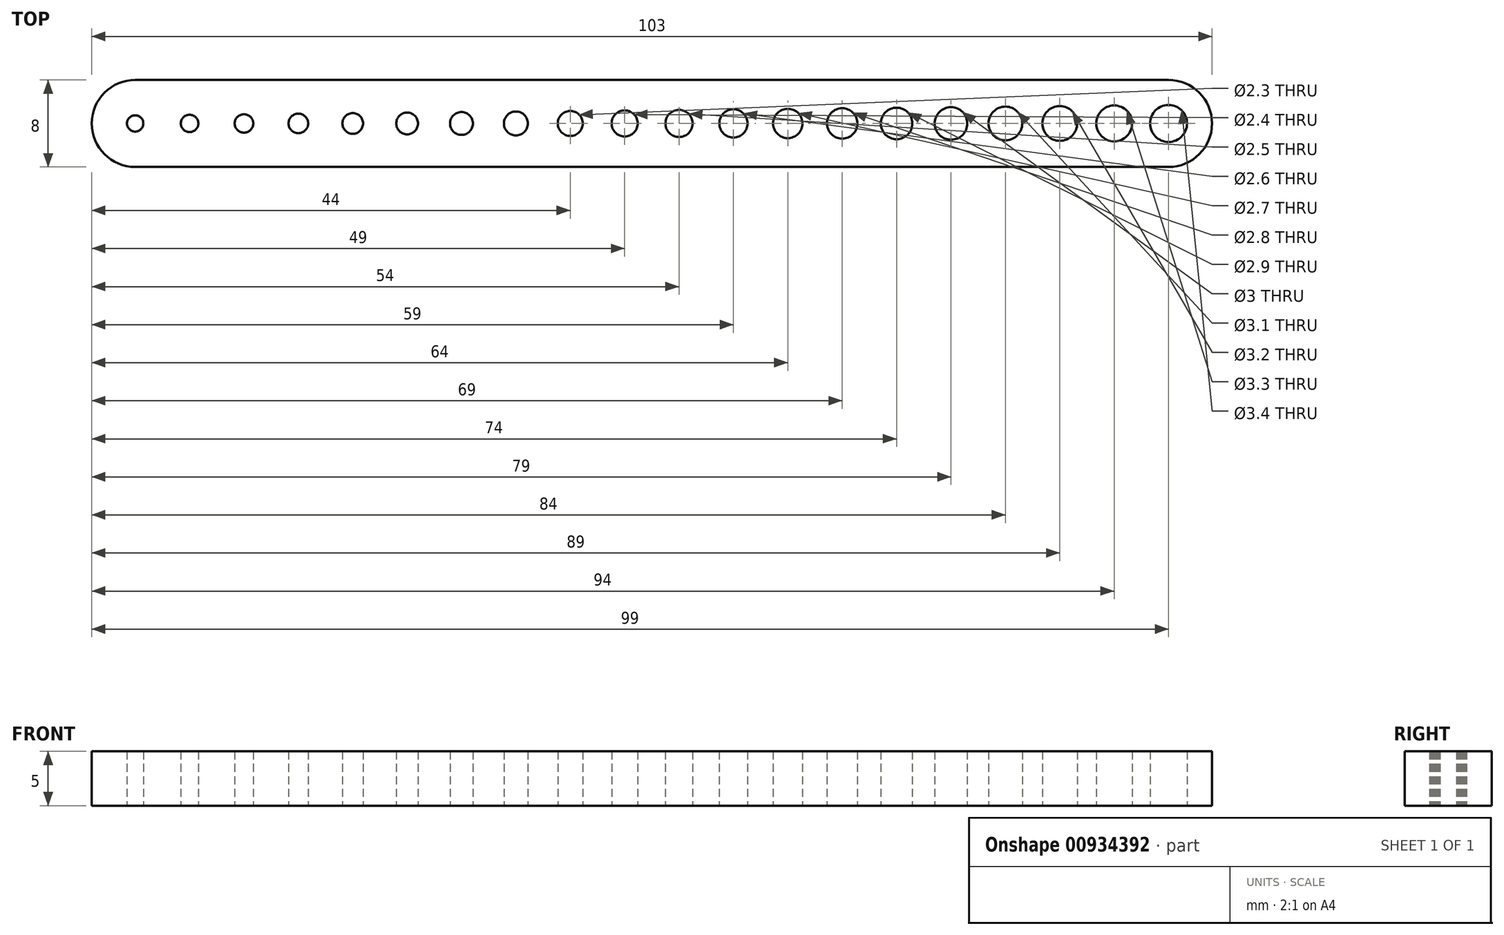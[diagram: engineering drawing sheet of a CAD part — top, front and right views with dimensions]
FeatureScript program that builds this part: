
annotation { "Feature Type Name" : "Feature", "Feature Type Description" : "" }
export const myFeature = defineFeature(function(context is Context, id is Id, definition is map)
    precondition{}
    {
        {
            var Q0;
            Q0=qCreatedBy(makeId("Top.planeOp"),FACE);
            var sketch = newSketch(context, id + "F0", { "sketchPlane" : qUnion([Q0])});
            skLineSegment(sketch, "E0.bottom", {"start": v(4, 0) * mm, "end": v(99, 0) * mm});
            skLineSegment(sketch, "E0.top", {"start": v(4, 8) * mm, "end": v(99, 8) * mm});
            skLineSegment(sketch, "E0.left", {"start": v(0, 4) * mm, "end": v(0, 4) * mm});
            skLineSegment(sketch, "E0.right", {"start": v(103, 4) * mm, "end": v(103, 4) * mm});
            skPoint(sketch, "E1.visualSharp", {"position": v(0, 8) * mm});
            skArc(sketch, "E1.filletArc", {"start": v(4, 8) * mm, "mid": v(1.17, 6.83) * mm, "end": v(0, 4) * mm});
            skPoint(sketch, "E2.visualSharp", {"position": v(0, 0) * mm});
            skArc(sketch, "E2.filletArc", {"start": v(0, 4) * mm, "mid": v(1.17, 1.17) * mm, "end": v(4, 0) * mm});
            skPoint(sketch, "E3.visualSharp", {"position": v(103, 8) * mm});
            skArc(sketch, "E3.filletArc", {"start": v(103, 4) * mm, "mid": v(101.83, 6.83) * mm, "end": v(99, 8) * mm});
            skPoint(sketch, "E4.visualSharp", {"position": v(103, 0) * mm});
            skArc(sketch, "E4.filletArc", {"start": v(99, 0) * mm, "mid": v(101.83, 1.17) * mm, "end": v(103, 4) * mm});
            skLineSegment(sketch, "E5", {"start": v(99, 4) * mm, "end": v(4, 4) * mm, "construction": true});
            skLineSegment(sketch, "E6", {"start": v(4, 4) * mm, "end": v(9, 4) * mm, "construction": true});
            skLineSegment(sketch, "E7", {"start": v(9, 4) * mm, "end": v(14, 4) * mm, "construction": true});
            skLineSegment(sketch, "E8", {"start": v(14, 4) * mm, "end": v(19, 4) * mm, "construction": true});
            skLineSegment(sketch, "E9", {"start": v(19, 4) * mm, "end": v(24, 4) * mm, "construction": true});
            skLineSegment(sketch, "E10", {"start": v(24, 4) * mm, "end": v(29, 4) * mm, "construction": true});
            skLineSegment(sketch, "E11", {"start": v(29, 4) * mm, "end": v(34, 4) * mm, "construction": true});
            skLineSegment(sketch, "E12", {"start": v(34, 4) * mm, "end": v(39, 4) * mm, "construction": true});
            skLineSegment(sketch, "E13", {"start": v(39, 4) * mm, "end": v(44, 4) * mm, "construction": true});
            skLineSegment(sketch, "E14", {"start": v(44, 4) * mm, "end": v(49, 4) * mm, "construction": true});
            skLineSegment(sketch, "E15", {"start": v(49, 4) * mm, "end": v(54, 4) * mm, "construction": true});
            skLineSegment(sketch, "E16", {"start": v(54, 4) * mm, "end": v(59, 4) * mm, "construction": true});
            skLineSegment(sketch, "E17", {"start": v(59, 4) * mm, "end": v(64, 4) * mm, "construction": true});
            skLineSegment(sketch, "E18", {"start": v(64, 4) * mm, "end": v(69, 4) * mm, "construction": true});
            skLineSegment(sketch, "E19", {"start": v(69, 4) * mm, "end": v(74, 4) * mm, "construction": true});
            skLineSegment(sketch, "E20", {"start": v(74, 4) * mm, "end": v(79, 4) * mm, "construction": true});
            skLineSegment(sketch, "E21", {"start": v(79, 4) * mm, "end": v(84, 4) * mm, "construction": true});
            skLineSegment(sketch, "E22", {"start": v(84, 4) * mm, "end": v(89, 4) * mm, "construction": true});
            skLineSegment(sketch, "E23", {"start": v(89, 4) * mm, "end": v(94, 4) * mm, "construction": true});
            skCircle(sketch, "E24", {"center": v(4, 4) * mm, "radius": 0.75 * mm});
            skCircle(sketch, "E25", {"center": v(99, 4) * mm, "radius": 1.7 * mm});
            skLineSegment(sketch, "E26", {"start": v(99, 4) * mm, "end": v(99, 8) * mm, "construction": true});
            skLineSegment(sketch, "E27", {"start": v(94, 4) * mm, "end": v(94, 8) * mm, "construction": true});
            skLineSegment(sketch, "E28", {"start": v(94, 8) * mm, "end": v(89, 8) * mm});
            skLineSegment(sketch, "E29", {"start": v(89, 8) * mm, "end": v(89, 4) * mm, "construction": true});
            skLineSegment(sketch, "E30", {"start": v(84, 4) * mm, "end": v(84, 8) * mm, "construction": true});
            skLineSegment(sketch, "E31", {"start": v(84, 8) * mm, "end": v(79, 8) * mm});
            skLineSegment(sketch, "E32", {"start": v(79, 8) * mm, "end": v(79, 4) * mm, "construction": true});
            skLineSegment(sketch, "E33", {"start": v(74, 4) * mm, "end": v(74, 8) * mm, "construction": true});
            skLineSegment(sketch, "E34", {"start": v(74, 8) * mm, "end": v(69, 8) * mm});
            skLineSegment(sketch, "E35", {"start": v(69, 8) * mm, "end": v(69, 4) * mm, "construction": true});
            skLineSegment(sketch, "E36", {"start": v(64, 4) * mm, "end": v(64, 8) * mm, "construction": true});
            skLineSegment(sketch, "E37", {"start": v(64, 8) * mm, "end": v(59, 8) * mm});
            skLineSegment(sketch, "E38", {"start": v(59, 8) * mm, "end": v(59, 4) * mm, "construction": true});
            skLineSegment(sketch, "E39", {"start": v(54, 4) * mm, "end": v(54, 8) * mm, "construction": true});
            skLineSegment(sketch, "E40", {"start": v(54, 8) * mm, "end": v(49, 8) * mm});
            skLineSegment(sketch, "E41", {"start": v(49, 8) * mm, "end": v(49, 4) * mm, "construction": true});
            skLineSegment(sketch, "E42", {"start": v(44, 4) * mm, "end": v(44, 8) * mm, "construction": true});
            skLineSegment(sketch, "E43", {"start": v(44, 8) * mm, "end": v(39, 8) * mm});
            skLineSegment(sketch, "E44", {"start": v(39, 8) * mm, "end": v(39, 4) * mm, "construction": true});
            skLineSegment(sketch, "E45", {"start": v(34, 4) * mm, "end": v(34, 8) * mm, "construction": true});
            skLineSegment(sketch, "E46", {"start": v(34, 8) * mm, "end": v(29, 8) * mm});
            skLineSegment(sketch, "E47", {"start": v(29, 8) * mm, "end": v(29, 4) * mm, "construction": true});
            skLineSegment(sketch, "E48", {"start": v(24, 4) * mm, "end": v(24, 8) * mm, "construction": true});
            skLineSegment(sketch, "E49", {"start": v(24, 8) * mm, "end": v(19, 8) * mm});
            skLineSegment(sketch, "E50", {"start": v(19, 8) * mm, "end": v(19, 4) * mm, "construction": true});
            skLineSegment(sketch, "E51", {"start": v(14, 4) * mm, "end": v(14, 8) * mm, "construction": true});
            skLineSegment(sketch, "E52", {"start": v(14, 8) * mm, "end": v(9, 8) * mm});
            skLineSegment(sketch, "E53", {"start": v(9, 8) * mm, "end": v(9, 4) * mm, "construction": true});
            skLineSegment(sketch, "E54", {"start": v(4, 4) * mm, "end": v(4, 8) * mm, "construction": true});
            skLineSegment(sketch, "E55", {"start": v(4, 4.75) * mm, "end": v(99, 5.7) * mm, "construction": true});
            skCircle(sketch, "E56", {"center": v(94, 4) * mm, "radius": 1.65 * mm});
            skCircle(sketch, "E57", {"center": v(89, 4) * mm, "radius": 1.6 * mm});
            skCircle(sketch, "E58", {"center": v(84, 4) * mm, "radius": 1.55 * mm});
            skCircle(sketch, "E59", {"center": v(79, 4) * mm, "radius": 1.5 * mm});
            skCircle(sketch, "E60", {"center": v(74, 4) * mm, "radius": 1.45 * mm});
            skCircle(sketch, "E61", {"center": v(69, 4) * mm, "radius": 1.4 * mm});
            skCircle(sketch, "E62", {"center": v(64, 4) * mm, "radius": 1.35 * mm});
            skCircle(sketch, "E63", {"center": v(59, 4) * mm, "radius": 1.3 * mm});
            skCircle(sketch, "E64", {"center": v(54, 4) * mm, "radius": 1.25 * mm});
            skCircle(sketch, "E65", {"center": v(49, 4) * mm, "radius": 1.2 * mm});
            skCircle(sketch, "E66", {"center": v(44, 4) * mm, "radius": 1.15 * mm});
            skCircle(sketch, "E67", {"center": v(39, 4) * mm, "radius": 1.1 * mm});
            skCircle(sketch, "E68", {"center": v(34, 4) * mm, "radius": 1.05 * mm});
            skCircle(sketch, "E69", {"center": v(29, 4) * mm, "radius": 1 * mm});
            skCircle(sketch, "E70", {"center": v(24, 4) * mm, "radius": 0.95 * mm});
            skCircle(sketch, "E71", {"center": v(19, 4) * mm, "radius": 0.9 * mm});
            skCircle(sketch, "E72", {"center": v(14, 4) * mm, "radius": 0.85 * mm});
            skCircle(sketch, "E73", {"center": v(9, 4) * mm, "radius": 0.8 * mm});
            skSolve(sketch);
        }
        {
            var Q0;
            Q0 = qSketchRegion(id + "F0", true);
            var Q1;
            {var subQ0=sQuery(id+"F0.wireOp",EDGE,"E24");var subQ1=sQuery(id+"F0.wireOp",EDGE,"E6");var subQ2=makeQuery(id+"F0.imprint","INTERSECT",VERTEX,{"derivedFrom":[subQ1,subQ0]});Q1=makeQuery(id+"F0.imprint","IMPRINT",FACE,{"disambiguationData":[TD([[makeQuery(id+"F0.imprint","IMPRINT",EDGE,{"disambiguationData":[TD([[subQ2,-1.0]])],"derivedFrom":subQ1}),1.0]])]});}
            var Q2;
            {var subQ1=sQuery(id+"F0.wireOp",EDGE,"E7");var subQ7=sQuery(id+"F0.wireOp",EDGE,"E73");var subQ9=makeQuery(id+"F0.imprint","INTERSECT",VERTEX,{"derivedFrom":[subQ1,subQ7]});Q2=makeQuery(id+"F0.imprint","IMPRINT",FACE,{"disambiguationData":[TD([[makeQuery(id+"F0.imprint","IMPRINT",EDGE,{"disambiguationData":[TD([[subQ9,-1.0]])],"derivedFrom":subQ1}),1.0]])]});}
            var Q3;
            {var subQ5=sQuery(id+"F0.wireOp",EDGE,"E72");var subQ7=sQuery(id+"F0.wireOp",EDGE,"E8");var subQ8=makeQuery(id+"F0.imprint","INTERSECT",VERTEX,{"derivedFrom":[subQ7,subQ5]});Q3=makeQuery(id+"F0.imprint","IMPRINT",FACE,{"disambiguationData":[TD([[makeQuery(id+"F0.imprint","IMPRINT",EDGE,{"disambiguationData":[TD([[subQ8,-1.0]])],"derivedFrom":subQ7}),1.0]])]});}
            var Q4;
            {var subQ1=sQuery(id+"F0.wireOp",EDGE,"E9");var subQ7=sQuery(id+"F0.wireOp",EDGE,"E71");var subQ9=makeQuery(id+"F0.imprint","INTERSECT",VERTEX,{"derivedFrom":[subQ1,subQ7]});Q4=makeQuery(id+"F0.imprint","IMPRINT",FACE,{"disambiguationData":[TD([[makeQuery(id+"F0.imprint","IMPRINT",EDGE,{"disambiguationData":[TD([[subQ9,-1.0]])],"derivedFrom":subQ1}),1.0]])]});}
            var Q5;
            {var subQ1=sQuery(id+"F0.wireOp",EDGE,"E10");var subQ7=sQuery(id+"F0.wireOp",EDGE,"E70");var subQ9=makeQuery(id+"F0.imprint","INTERSECT",VERTEX,{"derivedFrom":[subQ1,subQ7]});Q5=makeQuery(id+"F0.imprint","IMPRINT",FACE,{"disambiguationData":[TD([[makeQuery(id+"F0.imprint","IMPRINT",EDGE,{"disambiguationData":[TD([[subQ9,-1.0]])],"derivedFrom":subQ1}),1.0]])]});}
            var Q6;
            {var subQ1=sQuery(id+"F0.wireOp",EDGE,"E11");var subQ7=sQuery(id+"F0.wireOp",EDGE,"E69");var subQ8=makeQuery(id+"F0.imprint","INTERSECT",VERTEX,{"derivedFrom":[subQ1,subQ7]});Q6=makeQuery(id+"F0.imprint","IMPRINT",FACE,{"disambiguationData":[TD([[makeQuery(id+"F0.imprint","IMPRINT",EDGE,{"disambiguationData":[TD([[subQ8,-1.0]])],"derivedFrom":subQ1}),1.0]])]});}
            var Q7;
            {var subQ1=sQuery(id+"F0.wireOp",EDGE,"E12");var subQ5=sQuery(id+"F0.wireOp",EDGE,"E68");var subQ9=makeQuery(id+"F0.imprint","INTERSECT",VERTEX,{"derivedFrom":[subQ1,subQ5]});Q7=makeQuery(id+"F0.imprint","IMPRINT",FACE,{"disambiguationData":[TD([[makeQuery(id+"F0.imprint","IMPRINT",EDGE,{"disambiguationData":[TD([[subQ9,-1.0]])],"derivedFrom":subQ1}),1.0]])]});}
            var Q8;
            {var subQ5=sQuery(id+"F0.wireOp",EDGE,"E13");var subQ7=sQuery(id+"F0.wireOp",EDGE,"E67");var subQ9=makeQuery(id+"F0.imprint","INTERSECT",VERTEX,{"derivedFrom":[subQ5,subQ7]});Q8=makeQuery(id+"F0.imprint","IMPRINT",FACE,{"disambiguationData":[TD([[makeQuery(id+"F0.imprint","IMPRINT",EDGE,{"disambiguationData":[TD([[subQ9,-1.0]])],"derivedFrom":subQ5}),1.0]])]});}
            var Q9;
            {var subQ1=sQuery(id+"F0.wireOp",EDGE,"E14");var subQ7=sQuery(id+"F0.wireOp",EDGE,"E66");var subQ9=makeQuery(id+"F0.imprint","INTERSECT",VERTEX,{"derivedFrom":[subQ1,subQ7]});Q9=makeQuery(id+"F0.imprint","IMPRINT",FACE,{"disambiguationData":[TD([[makeQuery(id+"F0.imprint","IMPRINT",EDGE,{"disambiguationData":[TD([[subQ9,-1.0]])],"derivedFrom":subQ1}),1.0]])]});}
            var Q10;
            {var subQ1=sQuery(id+"F0.wireOp",EDGE,"E15");var subQ7=sQuery(id+"F0.wireOp",EDGE,"E65");var subQ9=makeQuery(id+"F0.imprint","INTERSECT",VERTEX,{"derivedFrom":[subQ1,subQ7]});Q10=makeQuery(id+"F0.imprint","IMPRINT",FACE,{"disambiguationData":[TD([[makeQuery(id+"F0.imprint","IMPRINT",EDGE,{"disambiguationData":[TD([[subQ9,-1.0]])],"derivedFrom":subQ1}),1.0]])]});}
            var Q11;
            {var subQ1=sQuery(id+"F0.wireOp",EDGE,"E16");var subQ7=sQuery(id+"F0.wireOp",EDGE,"E64");var subQ9=makeQuery(id+"F0.imprint","INTERSECT",VERTEX,{"derivedFrom":[subQ1,subQ7]});Q11=makeQuery(id+"F0.imprint","IMPRINT",FACE,{"disambiguationData":[TD([[makeQuery(id+"F0.imprint","IMPRINT",EDGE,{"disambiguationData":[TD([[subQ9,-1.0]])],"derivedFrom":subQ1}),1.0]])]});}
            var Q12;
            {var subQ1=sQuery(id+"F0.wireOp",EDGE,"E17");var subQ7=sQuery(id+"F0.wireOp",EDGE,"E63");var subQ9=makeQuery(id+"F0.imprint","INTERSECT",VERTEX,{"derivedFrom":[subQ1,subQ7]});Q12=makeQuery(id+"F0.imprint","IMPRINT",FACE,{"disambiguationData":[TD([[makeQuery(id+"F0.imprint","IMPRINT",EDGE,{"disambiguationData":[TD([[subQ9,-1.0]])],"derivedFrom":subQ1}),1.0]])]});}
            var Q13;
            {var subQ5=sQuery(id+"F0.wireOp",EDGE,"E62");var subQ7=sQuery(id+"F0.wireOp",EDGE,"E18");var subQ9=makeQuery(id+"F0.imprint","INTERSECT",VERTEX,{"derivedFrom":[subQ7,subQ5]});Q13=makeQuery(id+"F0.imprint","IMPRINT",FACE,{"disambiguationData":[TD([[makeQuery(id+"F0.imprint","IMPRINT",EDGE,{"disambiguationData":[TD([[subQ9,-1.0]])],"derivedFrom":subQ7}),1.0]])]});}
            var Q14;
            {var subQ1=sQuery(id+"F0.wireOp",EDGE,"E19");var subQ5=sQuery(id+"F0.wireOp",EDGE,"E61");var subQ6=makeQuery(id+"F0.imprint","INTERSECT",VERTEX,{"derivedFrom":[subQ1,subQ5]});Q14=makeQuery(id+"F0.imprint","IMPRINT",FACE,{"disambiguationData":[TD([[makeQuery(id+"F0.imprint","IMPRINT",EDGE,{"disambiguationData":[TD([[subQ6,-1.0]])],"derivedFrom":subQ1}),1.0]])]});}
            var Q15;
            {var subQ1=sQuery(id+"F0.wireOp",EDGE,"E20");var subQ7=sQuery(id+"F0.wireOp",EDGE,"E60");var subQ9=makeQuery(id+"F0.imprint","INTERSECT",VERTEX,{"derivedFrom":[subQ1,subQ7]});Q15=makeQuery(id+"F0.imprint","IMPRINT",FACE,{"disambiguationData":[TD([[makeQuery(id+"F0.imprint","IMPRINT",EDGE,{"disambiguationData":[TD([[subQ9,-1.0]])],"derivedFrom":subQ1}),1.0]])]});}
            var Q16;
            {var subQ1=sQuery(id+"F0.wireOp",EDGE,"E21");var subQ7=sQuery(id+"F0.wireOp",EDGE,"E59");var subQ9=makeQuery(id+"F0.imprint","INTERSECT",VERTEX,{"derivedFrom":[subQ1,subQ7]});Q16=makeQuery(id+"F0.imprint","IMPRINT",FACE,{"disambiguationData":[TD([[makeQuery(id+"F0.imprint","IMPRINT",EDGE,{"disambiguationData":[TD([[subQ9,-1.0]])],"derivedFrom":subQ1}),1.0]])]});}
            var Q17;
            {var subQ1=sQuery(id+"F0.wireOp",EDGE,"E22");var subQ5=sQuery(id+"F0.wireOp",EDGE,"E58");var subQ9=makeQuery(id+"F0.imprint","INTERSECT",VERTEX,{"derivedFrom":[subQ1,subQ5]});Q17=makeQuery(id+"F0.imprint","IMPRINT",FACE,{"disambiguationData":[TD([[makeQuery(id+"F0.imprint","IMPRINT",EDGE,{"disambiguationData":[TD([[subQ9,-1.0]])],"derivedFrom":subQ1}),1.0]])]});}
            var Q18;
            {var subQ1=sQuery(id+"F0.wireOp",EDGE,"E23");var subQ7=sQuery(id+"F0.wireOp",EDGE,"E57");var subQ9=makeQuery(id+"F0.imprint","INTERSECT",VERTEX,{"derivedFrom":[subQ1,subQ7]});Q18=makeQuery(id+"F0.imprint","IMPRINT",FACE,{"disambiguationData":[TD([[makeQuery(id+"F0.imprint","IMPRINT",EDGE,{"disambiguationData":[TD([[subQ9,-1.0]])],"derivedFrom":subQ1}),1.0]])]});}
            var Q19;
            {var subQ0=sQuery(id+"F0.wireOp",EDGE,"E25");var subQ1=sQuery(id+"F0.wireOp",EDGE,"E5");var subQ2=makeQuery(id+"F0.imprint","INTERSECT",VERTEX,{"derivedFrom":[subQ1,subQ0]});Q19=makeQuery(id+"F0.imprint","IMPRINT",FACE,{"disambiguationData":[TD([[makeQuery(id+"F0.imprint","IMPRINT",EDGE,{"disambiguationData":[TD([[subQ2,-1.0]])],"derivedFrom":subQ1}),-1.0]])]});}
            extrude(context, id + "F1", {"entities" : qUnion([Q0, Q1, Q2, Q3, Q4, Q5, Q6, Q7, Q8, Q9, Q10, Q11, Q12, Q13, Q14, Q15, Q16, Q17, Q18, Q19]), "depth" : 5 * mm, "offsetDistance" : 25 * mm});
        }
    });
